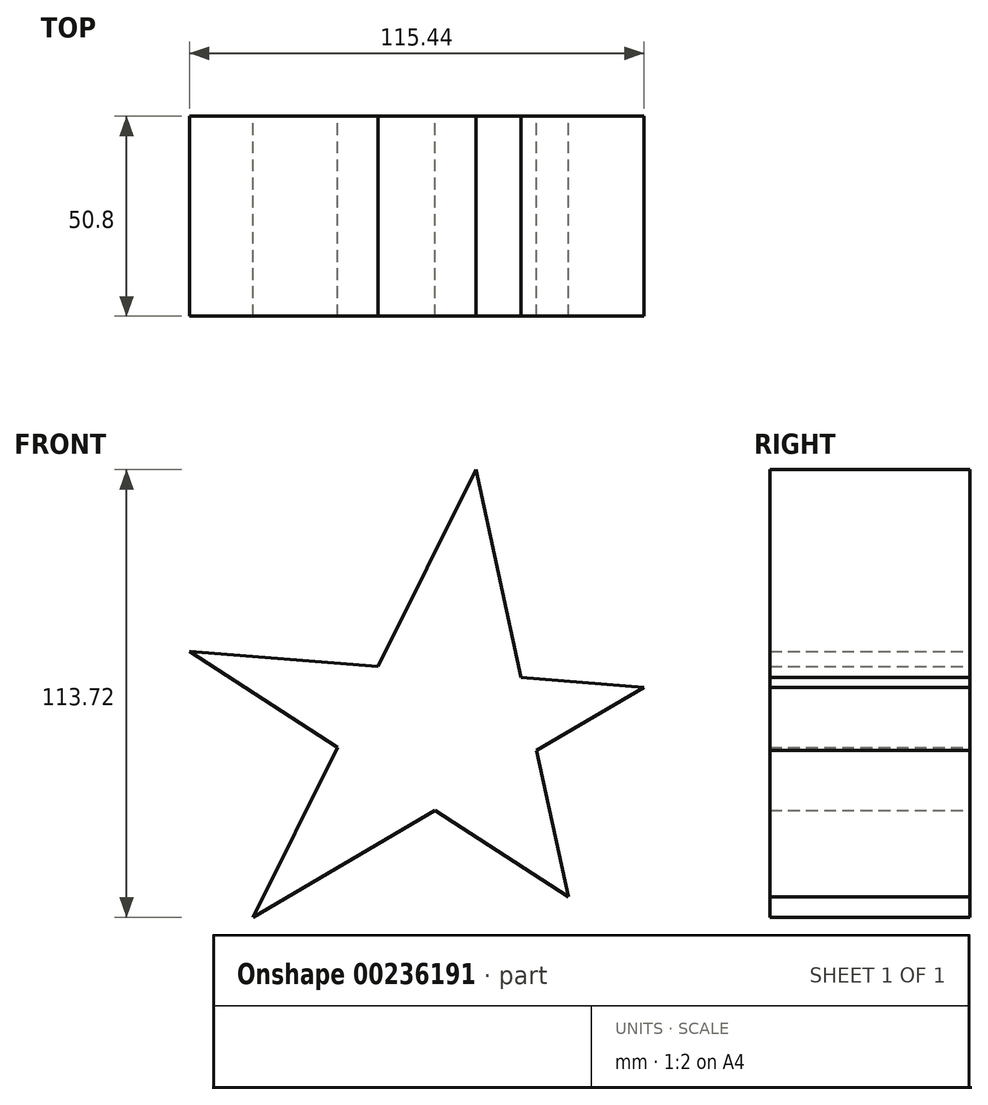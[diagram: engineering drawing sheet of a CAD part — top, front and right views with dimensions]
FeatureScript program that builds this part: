
annotation { "Feature Type Name" : "Feature", "Feature Type Description" : "" }
export const myFeature = defineFeature(function(context is Context, id is Id, definition is map)
    precondition{}
    {
        {
            var Q0;
            Q0=qCreatedBy(makeId("Front.planeOp"),FACE);
            var sketch = newSketch(context, id + "F0", { "sketchPlane" : qUnion([Q0])});
            skLineSegment(sketch, "E0", {"start": v(-6.34, 55.3) * mm, "end": v(-62.97, -58.42) * mm});
            skLineSegment(sketch, "E1", {"start": v(-62.97, -58.42) * mm, "end": v(36.37, 0) * mm});
            skLineSegment(sketch, "E2", {"start": v(36.37, 0) * mm, "end": v(-79.07, 9.16) * mm});
            skLineSegment(sketch, "E3", {"start": v(-79.07, 9.16) * mm, "end": v(17.2, -53.27) * mm});
            skLineSegment(sketch, "E4", {"start": v(17.2, -53.27) * mm, "end": v(-6.34, 55.3) * mm});
            skSolve(sketch);
        }
        {
            var Q0;
            {var subQ0=sQuery(id+"F0.wireOp",EDGE,"E4");var subQ1=sQuery(id+"F0.wireOp",EDGE,"E0");var subQ2=makeQuery(id+"F0.imprint","INTERSECT",VERTEX,{"derivedFrom":[subQ1,subQ0]});Q0=makeQuery(id+"F0.imprint","IMPRINT",FACE,{"disambiguationData":[TD([[makeQuery(id+"F0.imprint","IMPRINT",EDGE,{"disambiguationData":[TD([[subQ2,-1.0]])],"derivedFrom":subQ1}),1.0]])]});}
            var Q1;
            {var subQ1=sQuery(id+"F0.wireOp",EDGE,"E0");var subQ5=sQuery(id+"F0.wireOp",EDGE,"E2");var subQ6=makeQuery(id+"F0.imprint","INTERSECT",VERTEX,{"derivedFrom":[subQ1,subQ5]});Q1=makeQuery(id+"F0.imprint","IMPRINT",FACE,{"disambiguationData":[TD([[makeQuery(id+"F0.imprint","IMPRINT",EDGE,{"disambiguationData":[TD([[subQ6,-1.0]])],"derivedFrom":subQ1}),1.0]])]});}
            var Q2;
            {var subQ0=sQuery(id+"F0.wireOp",EDGE,"E2");var subQ1=sQuery(id+"F0.wireOp",EDGE,"E0");var subQ2=makeQuery(id+"F0.imprint","INTERSECT",VERTEX,{"derivedFrom":[subQ1,subQ0]});Q2=makeQuery(id+"F0.imprint","IMPRINT",FACE,{"disambiguationData":[TD([[makeQuery(id+"F0.imprint","IMPRINT",EDGE,{"disambiguationData":[TD([[subQ2,-1.0]])],"derivedFrom":subQ1}),-1.0]])]});}
            var Q3;
            {var subQ0=sQuery(id+"F0.wireOp",EDGE,"E1");var subQ1=sQuery(id+"F0.wireOp",EDGE,"E0");var subQ2=makeQuery(id+"F0.imprint","INTERSECT",VERTEX,{"derivedFrom":[subQ1,subQ0]});Q3=makeQuery(id+"F0.imprint","IMPRINT",FACE,{"disambiguationData":[TD([[makeQuery(id+"F0.imprint","IMPRINT",EDGE,{"disambiguationData":[TD([[subQ2,1.0]])],"derivedFrom":subQ1}),1.0]])]});}
            var Q4;
            {var subQ0=sQuery(id+"F0.wireOp",EDGE,"E3");var subQ1=sQuery(id+"F0.wireOp",EDGE,"E1");var subQ2=makeQuery(id+"F0.imprint","INTERSECT",VERTEX,{"derivedFrom":[subQ1,subQ0]});Q4=makeQuery(id+"F0.imprint","IMPRINT",FACE,{"disambiguationData":[TD([[makeQuery(id+"F0.imprint","IMPRINT",EDGE,{"disambiguationData":[TD([[subQ2,-1.0]])],"derivedFrom":subQ1}),-1.0]])]});}
            var Q5;
            {var subQ0=sQuery(id+"F0.wireOp",EDGE,"E2");var subQ1=sQuery(id+"F0.wireOp",EDGE,"E1");var subQ2=makeQuery(id+"F0.imprint","INTERSECT",VERTEX,{"derivedFrom":[subQ1,subQ0]});Q5=makeQuery(id+"F0.imprint","IMPRINT",FACE,{"disambiguationData":[TD([[makeQuery(id+"F0.imprint","IMPRINT",EDGE,{"disambiguationData":[TD([[subQ2,1.0]])],"derivedFrom":subQ1}),1.0]])]});}
            extrude(context, id + "F1", {"entities" : qUnion([Q0, Q1, Q2, Q3, Q4, Q5]), "depth" : 50.8 * mm});
        }
    });
